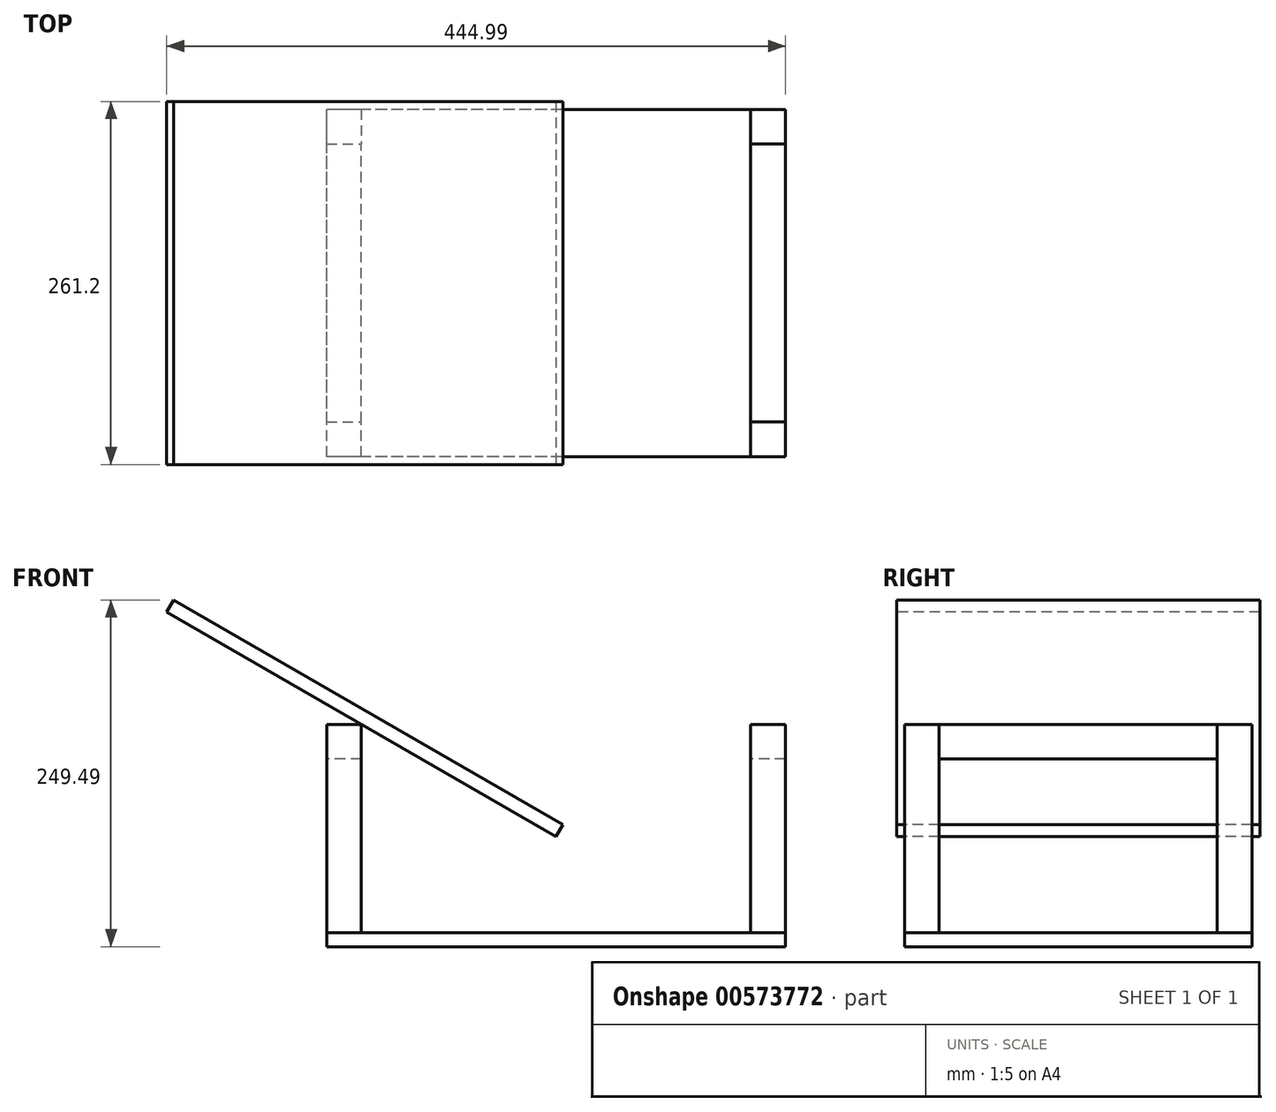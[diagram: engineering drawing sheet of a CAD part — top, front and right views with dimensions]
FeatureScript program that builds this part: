
annotation { "Feature Type Name" : "Feature", "Feature Type Description" : "" }
export const myFeature = defineFeature(function(context is Context, id is Id, definition is map)
    precondition{}
    {
        {
            var Q0;
            Q0=qCreatedBy(makeId("Top.planeOp"),FACE);
            var sketch = newSketch(context, id + "F0", { "sketchPlane" : qUnion([Q0])});
            skLineSegment(sketch, "E0.bottom", {"start": v(165, -125) * mm, "end": v(-165, -125) * mm});
            skLineSegment(sketch, "E0.top", {"start": v(165, 125) * mm, "end": v(-165, 125) * mm});
            skLineSegment(sketch, "E0.left", {"start": v(165, -125) * mm, "end": v(165, 125) * mm});
            skLineSegment(sketch, "E0.right", {"start": v(-165, -125) * mm, "end": v(-165, 125) * mm});
            skPoint(sketch, "E0.middle", {"position": v(0, 0) * mm});
            skLineSegment(sketch, "E1", {"start": v(0, 0) * mm, "end": v(0, -311) * mm, "construction": true});
            skPoint(sketch, "E1.endSnap0", {"position": v(0, -125) * mm});
            skLineSegment(sketch, "E2", {"start": v(0, 0) * mm, "end": v(0, 347.76) * mm, "construction": true});
            skSolve(sketch);
        }
        {
            var Q0;
            Q0=makeQuery(id+"F0.imprint","IMPRINT",FACE,{"disambiguationData":[TD([[makeQuery(id+"F0.imprint","IMPRINT",EDGE,{"derivedFrom":sQuery(id+"F0.wireOp",EDGE,"E0.bottom")}),-1.0]])]});
            extrude(context, id + "F1", {"entities" : qUnion([Q0]), "depth" : 10 * mm, "offsetDistance" : 25 * mm});
        }
        {
            var Q0;
            Q0=makeQuery(id+"F1.opExtrude","CAP_FACE",FACE,{"disambiguationData":[OSD([sQuery(id+"F0.wireOp",EDGE,"E0.bottom"),sQuery(id+"F0.wireOp",EDGE,"E0.top"),sQuery(id+"F0.wireOp",EDGE,"E0.left"),sQuery(id+"F0.wireOp",EDGE,"E0.right")])],"isStart":false});
            var sketch = newSketch(context, id + "F2", { "sketchPlane" : qUnion([Q0])});
            skLineSegment(sketch, "E3.bottom", {"start": v(-165, 125) * mm, "end": v(-140, 125) * mm});
            skLineSegment(sketch, "E3.top", {"start": v(-165, 100) * mm, "end": v(-140, 100) * mm});
            skLineSegment(sketch, "E3.left", {"start": v(-165, 125) * mm, "end": v(-165, 100) * mm});
            skLineSegment(sketch, "E3.right", {"start": v(-140, 125) * mm, "end": v(-140, 100) * mm});
            skLineSegment(sketch, "E4.bottom", {"start": v(-165, -125) * mm, "end": v(-140, -125) * mm});
            skLineSegment(sketch, "E4.top", {"start": v(-165, -100) * mm, "end": v(-140, -100) * mm});
            skLineSegment(sketch, "E4.left", {"start": v(-165, -125) * mm, "end": v(-165, -100) * mm});
            skLineSegment(sketch, "E4.right", {"start": v(-140, -125) * mm, "end": v(-140, -100) * mm});
            skLineSegment(sketch, "E5.bottom", {"start": v(165, -125) * mm, "end": v(140, -125) * mm});
            skLineSegment(sketch, "E5.top", {"start": v(165, -100) * mm, "end": v(140, -100) * mm});
            skLineSegment(sketch, "E5.left", {"start": v(165, -125) * mm, "end": v(165, -100) * mm});
            skLineSegment(sketch, "E5.right", {"start": v(140, -125) * mm, "end": v(140, -100) * mm});
            skLineSegment(sketch, "E6.bottom", {"start": v(165, 125) * mm, "end": v(140, 125) * mm});
            skLineSegment(sketch, "E6.top", {"start": v(165, 100) * mm, "end": v(140, 100) * mm});
            skLineSegment(sketch, "E6.left", {"start": v(165, 125) * mm, "end": v(165, 100) * mm});
            skLineSegment(sketch, "E6.right", {"start": v(140, 125) * mm, "end": v(140, 100) * mm});
            skSolve(sketch);
        }
        {
            var Q0;
            Q0=makeQuery(id+"F2.imprint","IMPRINT",FACE,{"disambiguationData":[TD([[makeQuery(id+"F2.imprint","IMPRINT",EDGE,{"derivedFrom":sQuery(id+"F2.wireOp",EDGE,"E6.bottom")}),1.0]])]});
            var Q1;
            Q1=makeQuery(id+"F2.imprint","IMPRINT",FACE,{"disambiguationData":[TD([[makeQuery(id+"F2.imprint","IMPRINT",EDGE,{"derivedFrom":sQuery(id+"F2.wireOp",EDGE,"E4.bottom")}),-1.0]])]});
            var Q2;
            Q2=makeQuery(id+"F2.imprint","IMPRINT",FACE,{"disambiguationData":[TD([[makeQuery(id+"F2.imprint","IMPRINT",EDGE,{"derivedFrom":sQuery(id+"F2.wireOp",EDGE,"E5.bottom")}),-1.0]])]});
            var Q3;
            Q3=makeQuery(id+"F2.imprint","IMPRINT",FACE,{"disambiguationData":[TD([[makeQuery(id+"F2.imprint","IMPRINT",EDGE,{"derivedFrom":sQuery(id+"F2.wireOp",EDGE,"E3.bottom")}),1.0]])]});
            extrude(context, id + "F3", {"entities" : qUnion([Q0, Q1, Q2, Q3]), "depth" : 150 * mm, "offsetDistance" : 25 * mm});
        }
        {
            var Q0;
            Q0=makeQuery(id+"F3.opExtrude","SWEPT_FACE",FACE,{"disambiguationData":[OSD([sQuery(id+"F2.wireOp",EDGE,"E6.top")])]});
            var sketch = newSketch(context, id + "F4", { "sketchPlane" : qUnion([Q0])});
            skLineSegment(sketch, "E7.bottom", {"start": v(165, 160) * mm, "end": v(140, 160) * mm});
            skLineSegment(sketch, "E7.top", {"start": v(165, 135) * mm, "end": v(140, 135) * mm});
            skLineSegment(sketch, "E7.left", {"start": v(165, 160) * mm, "end": v(165, 135) * mm});
            skLineSegment(sketch, "E7.right", {"start": v(140, 160) * mm, "end": v(140, 135) * mm});
            skSolve(sketch);
        }
        {
            var Q0;
            Q0=makeQuery(id+"F4.imprint","IMPRINT",FACE,{"disambiguationData":[TD([[makeQuery(id+"F4.imprint","IMPRINT",EDGE,{"derivedFrom":sQuery(id+"F4.wireOp",EDGE,"E7.bottom")}),1.0]])]});
            extrude(context, id + "F5", {"entities" : qUnion([Q0]), "depth" : 200 * mm, "offsetDistance" : 25 * mm});
        }
        {
            var Q0;
            Q0=makeQuery(id+"F3.opExtrude","SWEPT_FACE",FACE,{"disambiguationData":[OSD([sQuery(id+"F2.wireOp",EDGE,"E3.top")])]});
            var sketch = newSketch(context, id + "F6", { "sketchPlane" : qUnion([Q0])});
            skLineSegment(sketch, "E8.bottom", {"start": v(-140, 160) * mm, "end": v(-165, 160) * mm});
            skLineSegment(sketch, "E8.top", {"start": v(-140, 135) * mm, "end": v(-165, 135) * mm});
            skLineSegment(sketch, "E8.left", {"start": v(-140, 160) * mm, "end": v(-140, 135) * mm});
            skLineSegment(sketch, "E8.right", {"start": v(-165, 160) * mm, "end": v(-165, 135) * mm});
            skSolve(sketch);
        }
        {
            var Q0;
            Q0=makeQuery(id+"F6.imprint","IMPRINT",FACE,{"disambiguationData":[TD([[makeQuery(id+"F6.imprint","IMPRINT",EDGE,{"derivedFrom":sQuery(id+"F6.wireOp",EDGE,"E8.bottom")}),-1.0]])]});
            extrude(context, id + "F7", {"entities" : qUnion([Q0]), "depth" : 200 * mm, "offsetDistance" : 25 * mm});
        }
        {
            var Q0;
            Q0=makeQuery(id+"F5.opExtrude","SWEPT_EDGE",EDGE,{"disambiguationData":[OSD([sQuery(id+"F4.wireOp",EDGE,"E7.bottom"),sQuery(id+"F4.wireOp",EDGE,"E7.right")])]});
            cPlane(context, id + "F8", {"entities" : qUnion([Q0]), "cplaneType" : CPlaneType.LINE_ANGLE, "offset" : 25 * mm, "angle" : 30 * degree, "oppositeDirection" : true, "width" : 150 * mm, "height" : 150 * mm});
        }
        {
            var Q0;
            Q0=makeQuery(id+"F7.opExtrude","SWEPT_EDGE",EDGE,{"disambiguationData":[OSD([sQuery(id+"F6.wireOp",EDGE,"E8.bottom"),sQuery(id+"F6.wireOp",EDGE,"E8.left")])]});
            cPlane(context, id + "F9", {"entities" : qUnion([Q0]), "cplaneType" : CPlaneType.LINE_ANGLE, "offset" : 25 * mm, "angle" : 30 * degree, "width" : 150 * mm, "height" : 150 * mm});
        }
        {
            var Q0;
            Q0=qCreatedBy(id+"F9.planeOp",FACE);
            var sketch = newSketch(context, id + "F10", { "sketchPlane" : qUnion([Q0])});
            skLineSegment(sketch, "E9.bottom", {"start": v(-39.6, 130.6) * mm, "end": v(-362.9, 130.6) * mm});
            skLineSegment(sketch, "E9.top", {"start": v(-39.6, -130.6) * mm, "end": v(-362.9, -130.6) * mm});
            skLineSegment(sketch, "E9.left", {"start": v(-39.6, 130.6) * mm, "end": v(-39.6, -130.6) * mm});
            skLineSegment(sketch, "E9.right", {"start": v(-362.9, 130.6) * mm, "end": v(-362.9, -130.6) * mm});
            skPoint(sketch, "E9.middle", {"position": v(-201.24, 0) * mm});
            skSolve(sketch);
        }
        {
            var Q0;
            Q0=makeQuery(id+"F10.imprint","IMPRINT",FACE,{"disambiguationData":[TD([[makeQuery(id+"F10.imprint","IMPRINT",EDGE,{"derivedFrom":sQuery(id+"F10.wireOp",EDGE,"E9.bottom")}),1.0]])]});
            extrude(context, id + "F11", {"entities" : qUnion([Q0]), "depth" : 10 * mm, "offsetDistance" : 25 * mm});
        }
    });
